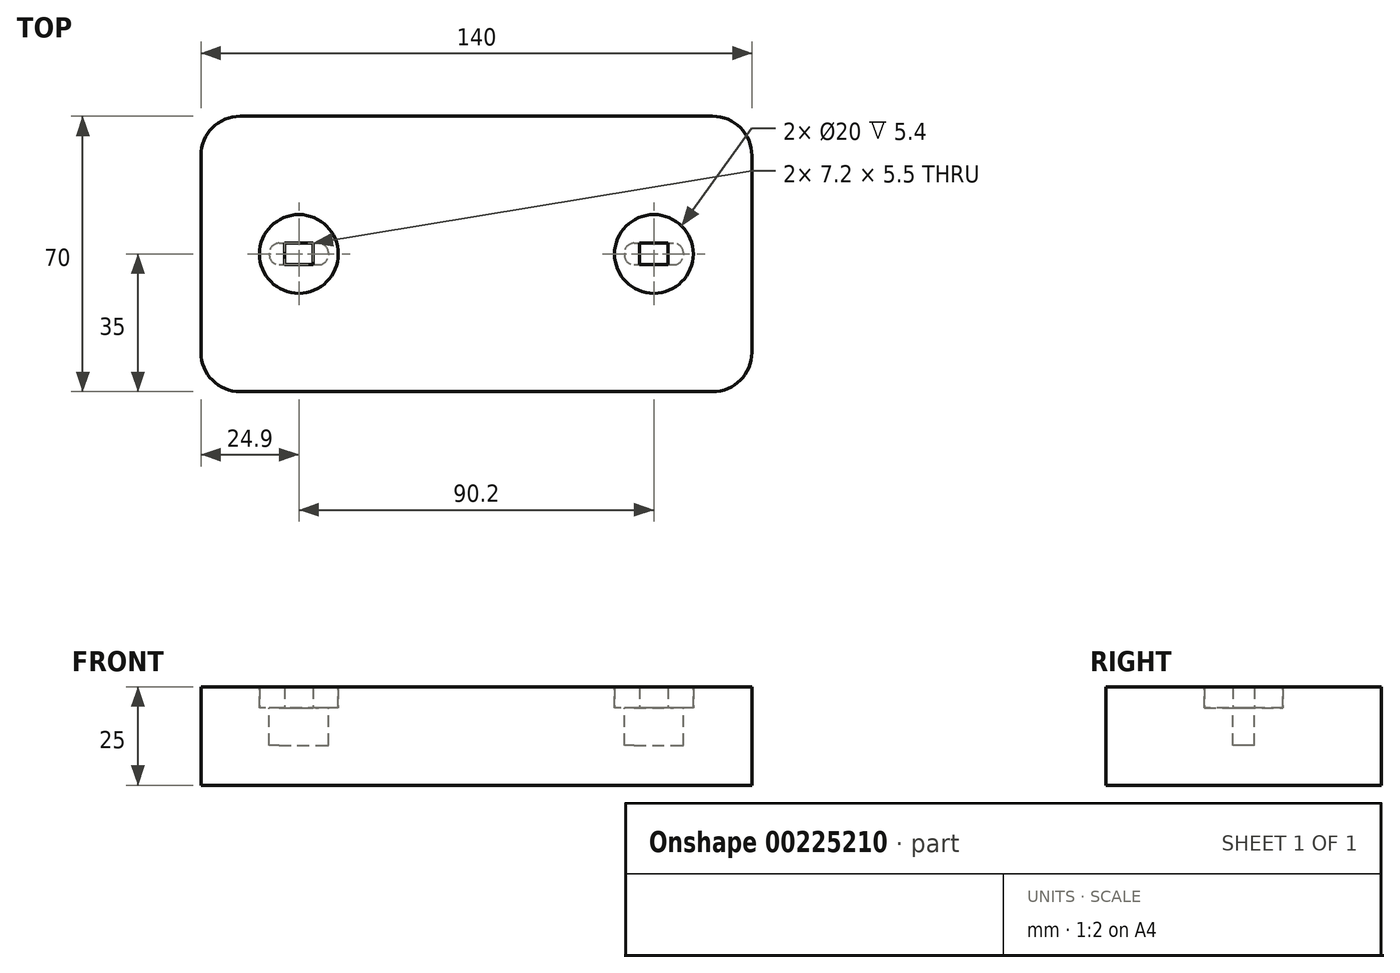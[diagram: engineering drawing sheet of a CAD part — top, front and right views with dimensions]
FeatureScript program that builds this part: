
annotation { "Feature Type Name" : "Feature", "Feature Type Description" : "" }
export const myFeature = defineFeature(function(context is Context, id is Id, definition is map)
    precondition{}
    {
        {
            var Q0;
            Q0=qCreatedBy(makeId("Top.planeOp"),FACE);
            var sketch = newSketch(context, id + "F0", { "sketchPlane" : qUnion([Q0])});
            skLineSegment(sketch, "E0.bottom", {"start": v(70, 35) * mm, "end": v(-70, 35) * mm});
            skLineSegment(sketch, "E0.top", {"start": v(70, -35) * mm, "end": v(-70, -35) * mm});
            skLineSegment(sketch, "E0.left", {"start": v(70, 35) * mm, "end": v(70, -35) * mm});
            skLineSegment(sketch, "E0.right", {"start": v(-70, 35) * mm, "end": v(-70, -35) * mm});
            skPoint(sketch, "E0.middle", {"position": v(0, 0) * mm});
            skSolve(sketch);
        }
        {
            var Q0;
            Q0=makeQuery(id+"F0.imprint","IMPRINT",FACE,{"disambiguationData":[TD([[makeQuery(id+"F0.imprint","IMPRINT",EDGE,{"derivedFrom":sQuery(id+"F0.wireOp",EDGE,"E0.bottom")}),1.0]])]});
            extrude(context, id + "F1", {"entities" : qUnion([Q0]), "depth" : 35 * mm});
        }
        {
            var Q0;
            Q0=makeQuery(id+"F1.opExtrude","SWEPT_EDGE",EDGE,{"disambiguationData":[OSD([sQuery(id+"F0.wireOp",EDGE,"E0.top"),sQuery(id+"F0.wireOp",EDGE,"E0.right")])]});
            var Q1;
            Q1=makeQuery(id+"F1.opExtrude","SWEPT_EDGE",EDGE,{"disambiguationData":[OSD([sQuery(id+"F0.wireOp",EDGE,"E0.top"),sQuery(id+"F0.wireOp",EDGE,"E0.left")])]});
            var Q2;
            Q2=makeQuery(id+"F1.opExtrude","SWEPT_EDGE",EDGE,{"disambiguationData":[OSD([sQuery(id+"F0.wireOp",EDGE,"E0.bottom"),sQuery(id+"F0.wireOp",EDGE,"E0.left")])]});
            var Q3;
            Q3=makeQuery(id+"F1.opExtrude","SWEPT_EDGE",EDGE,{"disambiguationData":[OSD([sQuery(id+"F0.wireOp",EDGE,"E0.bottom"),sQuery(id+"F0.wireOp",EDGE,"E0.right")])]});
            fillet(context, id + "F2", {"entities" : qUnion([Q0, Q1, Q2, Q3]), "radius" : 10 * mm, "tangentPropagation" : true, "allowEdgeOverflow" : false});
        }
        {
            var Q0;
            Q0=makeQuery(id+"F1.opExtrude","CAP_FACE",FACE,{"disambiguationData":[OSD([sQuery(id+"F0.wireOp",EDGE,"E0.bottom"),sQuery(id+"F0.wireOp",EDGE,"E0.top"),sQuery(id+"F0.wireOp",EDGE,"E0.left"),sQuery(id+"F0.wireOp",EDGE,"E0.right")])],"isStart":false});
            var sketch = newSketch(context, id + "F3", { "sketchPlane" : qUnion([Q0])});
            skCircle(sketch, "E1", {"center": v(-45.1, 0) * mm, "radius": 10 * mm});
            skCircle(sketch, "E2", {"center": v(45.1, 0) * mm, "radius": 10 * mm});
            skSolve(sketch);
        }
        {
            var Q0;
            Q0 = qSketchRegion(id + "F3", true);
            extrude(context, id + "F4", {"entities" : qUnion([Q0]), "operationType" : NewBodyOperationType.REMOVE, "oppositeDirection" : true, "depth" : 5.4 * mm});
        }
        {
            var Q0;
            Q0=makeQuery(id+"F4.boolean.opBoolean","COPY",FACE,{"derivedFrom":makeQuery(id+"F4.opExtrude","CAP_FACE",FACE,{"disambiguationData":[OSD([sQuery(id+"F3.wireOp",EDGE,"E1")])],"isStart":false})});
            var sketch = newSketch(context, id + "F5", { "sketchPlane" : qUnion([Q0])});
            skLineSegment(sketch, "E3.bottom", {"start": v(-50.1, 2.75) * mm, "end": v(-40.1, 2.75) * mm});
            skLineSegment(sketch, "E3.top", {"start": v(-50.1, -2.75) * mm, "end": v(-40.1, -2.75) * mm});
            skLineSegment(sketch, "E3.left", {"start": v(-52.6, 0.25) * mm, "end": v(-52.6, -0.25) * mm});
            skLineSegment(sketch, "E3.right", {"start": v(-37.6, 0.25) * mm, "end": v(-37.6, -0.25) * mm});
            skPoint(sketch, "E3.middle", {"position": v(-45.1, 0) * mm});
            skLineSegment(sketch, "E4.bottom", {"start": v(40.1, 2.75) * mm, "end": v(50.1, 2.75) * mm});
            skLineSegment(sketch, "E4.top", {"start": v(40.1, -2.75) * mm, "end": v(50.1, -2.75) * mm});
            skLineSegment(sketch, "E4.left", {"start": v(37.6, 0.25) * mm, "end": v(37.6, -0.25) * mm});
            skLineSegment(sketch, "E4.right", {"start": v(52.6, 0.25) * mm, "end": v(52.6, -0.25) * mm});
            skPoint(sketch, "E4.middle", {"position": v(45.1, 0) * mm});
            skPoint(sketch, "E5.visualSharp", {"position": v(-52.6, 2.75) * mm});
            skArc(sketch, "E5.filletArc", {"start": v(-50.1, 2.75) * mm, "mid": v(-51.87, 2.02) * mm, "end": v(-52.6, 0.25) * mm});
            skPoint(sketch, "E6.visualSharp", {"position": v(-52.6, -2.75) * mm});
            skArc(sketch, "E6.filletArc", {"start": v(-52.6, -0.25) * mm, "mid": v(-51.87, -2.02) * mm, "end": v(-50.1, -2.75) * mm});
            skPoint(sketch, "E7.visualSharp", {"position": v(-37.6, 2.75) * mm});
            skArc(sketch, "E7.filletArc", {"start": v(-37.6, 0.25) * mm, "mid": v(-38.33, 2.02) * mm, "end": v(-40.1, 2.75) * mm});
            skPoint(sketch, "E8.visualSharp", {"position": v(-37.6, -2.75) * mm});
            skArc(sketch, "E8.filletArc", {"start": v(-40.1, -2.75) * mm, "mid": v(-38.33, -2.02) * mm, "end": v(-37.6, -0.25) * mm});
            skPoint(sketch, "E9.visualSharp", {"position": v(37.6, -2.75) * mm});
            skArc(sketch, "E9.filletArc", {"start": v(37.6, -0.25) * mm, "mid": v(38.33, -2.02) * mm, "end": v(40.1, -2.75) * mm});
            skPoint(sketch, "E10.visualSharp", {"position": v(37.6, 2.75) * mm});
            skArc(sketch, "E10.filletArc", {"start": v(40.1, 2.75) * mm, "mid": v(38.33, 2.02) * mm, "end": v(37.6, 0.25) * mm});
            skPoint(sketch, "E11.visualSharp", {"position": v(52.6, 2.75) * mm});
            skArc(sketch, "E11.filletArc", {"start": v(52.6, 0.25) * mm, "mid": v(51.87, 2.02) * mm, "end": v(50.1, 2.75) * mm});
            skPoint(sketch, "E12.visualSharp", {"position": v(52.6, -2.75) * mm});
            skArc(sketch, "E12.filletArc", {"start": v(50.1, -2.75) * mm, "mid": v(51.87, -2.02) * mm, "end": v(52.6, -0.25) * mm});
            skCircle(sketch, "E13", {"center": v(45.1, 0) * mm, "radius": 10 * mm, "construction": true});
            skSolve(sketch);
        }
        {
            var Q0;
            Q0 = qSketchRegion(id + "F5", true);
            extrude(context, id + "F6", {"entities" : qUnion([Q0]), "operationType" : NewBodyOperationType.REMOVE, "oppositeDirection" : true, "depth" : 9.4 * mm});
        }
        {
            var Q0;
            Q0=makeQuery(id+"F4.boolean.opBoolean","COPY",FACE,{"derivedFrom":makeQuery(id+"F4.opExtrude","CAP_FACE",FACE,{"disambiguationData":[OSD([sQuery(id+"F3.wireOp",EDGE,"E1")])],"isStart":false})});
            var sketch = newSketch(context, id + "F7", { "sketchPlane" : qUnion([Q0])});
            skCircle(sketch, "E14", {"center": v(-45.1, 0) * mm, "radius": 10 * mm});
            skCircle(sketch, "E15.MirrorC", {"center": v(45.1, 0) * mm, "radius": 10 * mm});
            skLineSegment(sketch, "E16.bottom", {"start": v(-48.7, 2.75) * mm, "end": v(-41.5, 2.75) * mm});
            skLineSegment(sketch, "E16.top", {"start": v(-48.7, -2.75) * mm, "end": v(-41.5, -2.75) * mm});
            skLineSegment(sketch, "E16.left", {"start": v(-48.7, 2.75) * mm, "end": v(-48.7, -2.75) * mm});
            skLineSegment(sketch, "E16.right", {"start": v(-41.5, 2.75) * mm, "end": v(-41.5, -2.75) * mm});
            skLineSegment(sketch, "E17.MirrorCS", {"start": v(48.7, -2.75) * mm, "end": v(41.5, -2.75) * mm});
            skLineSegment(sketch, "E18.MirrorCS", {"start": v(48.7, 2.75) * mm, "end": v(48.7, -2.75) * mm});
            skLineSegment(sketch, "E19.MirrorCS", {"start": v(48.7, 2.75) * mm, "end": v(41.5, 2.75) * mm});
            skLineSegment(sketch, "E20.MirrorCS", {"start": v(41.5, 2.75) * mm, "end": v(41.5, -2.75) * mm});
            skLineSegment(sketch, "E21", {"start": v(-41.5, 2.75) * mm, "end": v(41.5, 2.75) * mm, "construction": true});
            skSolve(sketch);
        }
        {
            var Q0;
            Q0 = qSketchRegion(id + "F7", true);
            extrude(context, id + "F8", {"entities" : qUnion([Q0]), "depth" : 5.3 * mm});
        }
        {
            var Q0;
            Q0=makeQuery(id+"F1.opExtrude","CAP_FACE",FACE,{"disambiguationData":[OSD([sQuery(id+"F0.wireOp",EDGE,"E0.bottom"),sQuery(id+"F0.wireOp",EDGE,"E0.top"),sQuery(id+"F0.wireOp",EDGE,"E0.left"),sQuery(id+"F0.wireOp",EDGE,"E0.right")])],"isStart":true});
            var sketch = newSketch(context, id + "F9", { "sketchPlane" : qUnion([Q0])});
            skLineSegment(sketch, "E22.bottom", {"start": v(110.12, -59.35) * mm, "end": v(-94.9, -59.35) * mm});
            skLineSegment(sketch, "E22.top", {"start": v(110.12, 42.02) * mm, "end": v(-94.9, 42.02) * mm});
            skLineSegment(sketch, "E22.left", {"start": v(110.12, -59.35) * mm, "end": v(110.12, 42.02) * mm});
            skLineSegment(sketch, "E22.right", {"start": v(-94.9, -59.35) * mm, "end": v(-94.9, 42.02) * mm});
            skSolve(sketch);
        }
        {
            var Q0;
            Q0 = qSketchRegion(id + "F9", true);
            extrude(context, id + "F10", {"entities" : qUnion([Q0]), "operationType" : NewBodyOperationType.REMOVE, "oppositeDirection" : true, "depth" : 10 * mm, "offsetDistance" : 25 * mm});
        }
    });
